# Revit family: QF_HOSHIZAKI_IM-240DWNE-HC-32
name_source: partatom
category: Specialty Equipment
revit_build: Autodesk Revit 2016 (Build: 20150220_1215(x64)
units: mm (PartAtom-declared; Revit-internal decimal feet)

## family parameters
Always vertical = Yes
Cut with Voids When Loaded = No
OmniClass Number = 23.40.40.14
OmniClass Title = Food Service Equipment
Part Type = Normal
Room Calculation Point = No
Round Connector Dimension = Use Diameter
Shared = No
Work Plane-Based = No

## types (1)
- IM-240DWNE-HC-32_240V/1Ph/50Hz
    Accessory = No
    Apparent Power = 835 VA
    Assembly Code = E1090320
    BTUH = 0 W
    Cold Water Flow = 0.0 L/s
    Cold Water Size = 19 mm
    Cold Water Temperature Recommended = 0 °C
    Conn Conduit = No
    Cost = 0 $
    Cycle = 50 Hz
    Depth Actual = 700 mm  [stored 2.29659 ft]
    Description = STACKABLE CUBE ICE MAKER - ICE TYPE XL CUBE - 32 - 1084X700X500 MM
    Electric power = 835 W
    FL Amps = 3 A
    Height Actual = 500 mm  [stored 1.64042 ft]
    Indirect Waste Size = 19 mm
    Length Actual = 1084 mm  [stored 3.55643 ft]
    Manufacturer = HOSHIZAKI
    Max Overcurrent Protection = 0 A
    Min Ckt Ampacity = 0 A
    Model = IM-240DWNE-HC-32
    Number of Poles = 2
    Phase = 1
    Refrigerant Volume = 0.0 L/s
    Refrigeration Evaporation Temperature = 0 °C
    Refrigeration Liquid Line Size = 13 mm
    Refrigeration Suction Line Size = 13 mm
    URL = www.hoshizaki-europe.com
    Volts = 240 V
    Weight = 79.00 kg

note: [stored X ft] marks values corroborated as IEEE doubles in the binary element streams (Revit-internal decimal feet)

## geometry (parser evidence)
native form markers: Blend x10, Sweep x4
no freeform markers — native parametric forms only
